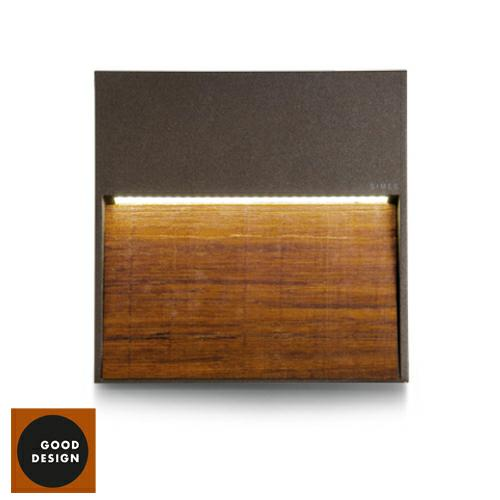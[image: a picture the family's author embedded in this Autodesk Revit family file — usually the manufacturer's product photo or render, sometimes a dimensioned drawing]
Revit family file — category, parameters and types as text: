
# Revit family: SIMES_L.9260W_Skill Wood
name_source: partatom
category: Lighting Fixtures
revit_build: Autodesk Revit 2016 (Build: 20150714_1515(x64)
units: mm (PartAtom-declared; Revit-internal decimal feet)

## family parameters
Cut with Voids When Loaded = No
Host = Face
Light Source = Yes
OmniClass Number = 23.80.70.14
OmniClass Title = Luminaries for External Lighting
Part Type = Normal
Room Calculation Point = No
Round Connector Dimension = Use Diameter
Shared = No

## types (1)
- SIMES_L.9260W_Skill Wood
    Approval mark = CE
    Assembly Code = D5020
    BIMobject category = Outside
    Brand url = http://www.simes.it
    Color Filter = 16777215
    Color Rendering Index = CRI 90
    Colour Temperature = 3000
    Control Gear = electronic transformer
    Default Elevation = 1219 mm
    Description = SKILL SQUARE WOOD
Art. L.9260W
MODULES LED 3000K  230V CRI 90 MacAdam step 3
Rated luminaire luminous flux: 312lm
Rated input power: 12.5W
Luminaire efficacy: 25lm/W
Electronic ballast 220÷240V 0/50/60Hz
CE

PRODUCT TYPE
Wall mounted luminaire. IP rating IP 65
MATERIAL CHARACTERISTICS
Aluminium die cast housing in EN AB-47100 (low copper content) with high resistance against corrosion. Oiled TEAK wood finish 8mm thick. Stone wash surface treatment prior to painting process. A4 grade Stainless Steel screws with 2,5-3% molybdenum content which increases the resistance against corrosion. Silicone gaskets. Painting Process : 3 Step Process
1) Surface treatment with BONDERITE. A heavy metal free chemical surface treatment containing ceramic nano particles giving a cohesive, inorganic and highly dense protective coating. 2) PRE POLYMERIZATION a process of introducing an epoxy primer with excellent characteristics to the paint which also offers very high resistance to oxidation due to its Zinc content. 3) POLYMERIZATION a process with the application of polyester powder with high resistance against UV rays and harsh weather conditions. Resistance test protection for Marine applications for 1200h.  Mechanical resistance IK 08
LIGHTING PERFORMANCE
Toughened glass diffuser. LOR -- 
WIRING
Luminaire hard wired with single neoprene cable (MINISKILL). Luminaire suitable for single grommet. 
MAINTENANCE
This product has been manufactured with hand crafted procedures, therefore small imperfections, subsidence of the wood surface, actual cracks and future, colour ripples and variations over time, are deliberately present and they are a feature of the wood, proving the hand-made manufacturing procedure.  
Isolation: CLASS I . Available colours: White (cod.01), BURNISHED BRONZE (cod.20). Weight: 1.2 Kg Glow Wire test: --
L.E.D circuit included.
SKILL WOOD PATENTED
This luminaire contains built-in LED modules with energy class: A, A+, A++. In case of damage or malfunction please contact the manufacturer to receive additional instructions on how to replace and relative spare parts to order. The LED modules cannot be handled in the luminaire by the end user (Regulation UE 874/2012).
LED circuit boards are engineered accordingly to actual Lumen Maintenance regulation (LM80) and Technical Memorandum (TM21) where uniformity and quality of light is 50.000 hours referred to L70  B20 Ta 25°C.Lifecycle refers to LED circuit boards only, all others components of the luminaire are excluded.

EMERGENCY VERSIONS The fittings operates both on AC ( 50/60Hz ) and DC ( 0Hz ) voltage.
    Design country = Italy
    Dimming Lamp Color Temperature Shift = <None>
    Edition number = 1
    Frequency = 0/50/60Hz
    IFC Classification = Light Fixture
    IK Rating = IK 08
    Installation instructions = http://www.simes.it
    Lamp = LED
    Lamp Light Flux = 970
    Lamp count = 1
    Last Update = 08/11/2018 15:13:23
    Lifetime = 50000 L70 B20 Ta 25°C
    Light Output Ratio = 100
    Luminous efficacy = 25
    Manufacturer = SIMES
    Manufacturer country = Italy
    Manufacturer name = Simes
    Masterformat 2014 Code = 26 56 00
    Masterformat 2014 Description = Exterior Lighting
    Material main = Aluminium
    Material secondary = Teak
    Model = L.9260W
    Mounting Place = Wall
    Mounting Type = Surface mounted
    NBS Reference Code = 49
    NBS Reference Description = Luminaries And Lamps
    Nominal height = 0
    Nominal width = 0
    OmniClass Code = 23-35 47 11
    OmniClass Description = Lighting Fixture
    Photometric Web File = L9260W.ies
    Product Group = wall-mounted luminaire
    Product Guid = fe495009-d019-4f6c-b847-0b62a99c5d17
    Product Name = Skill Wood
    Product SKU = SKILL_WOOD
    Product certification = http://www.simes.it
    Product data url = https://bimobject.com
    Product url = http://www.simes.it
    Protection Class = Protection class I
    Protection Degree = IP 65
    QR code = http://bimobject.com
    System Light Flux = 312
    System Power = 12,5
    Technical description = http://www.simes.it
    Tilt Angle = 90.00°
    Type Comments = SIMES S.p.A. - All rights reserved
    Type Image = skill-square-wood.jpg
    UNSPSC Code = 3911
    URL = http://www.simes.it
    Uniclass 1.4 Code = YJ73
    Uniclass 1.4 Description = Luminaries and lamps
    Uniclass 2.0 Code = PR-49
    Uniclass 2.0 Description = Luminaries and lamps
    Uniclass 2015 Code = EF_70_80
    Uniclass 2015 Name = Lighting
    Uniformat II Code = D5020
    Uniformat II Description = Lighting & Branch Wiring
    Voltage = 220÷240V
    Weight Net (Kg) = 0
    Youtube clip = http://www.simes.it

## geometry (parser evidence)
native form markers: Blend x2, Sweep x1
no freeform markers — native parametric forms only
